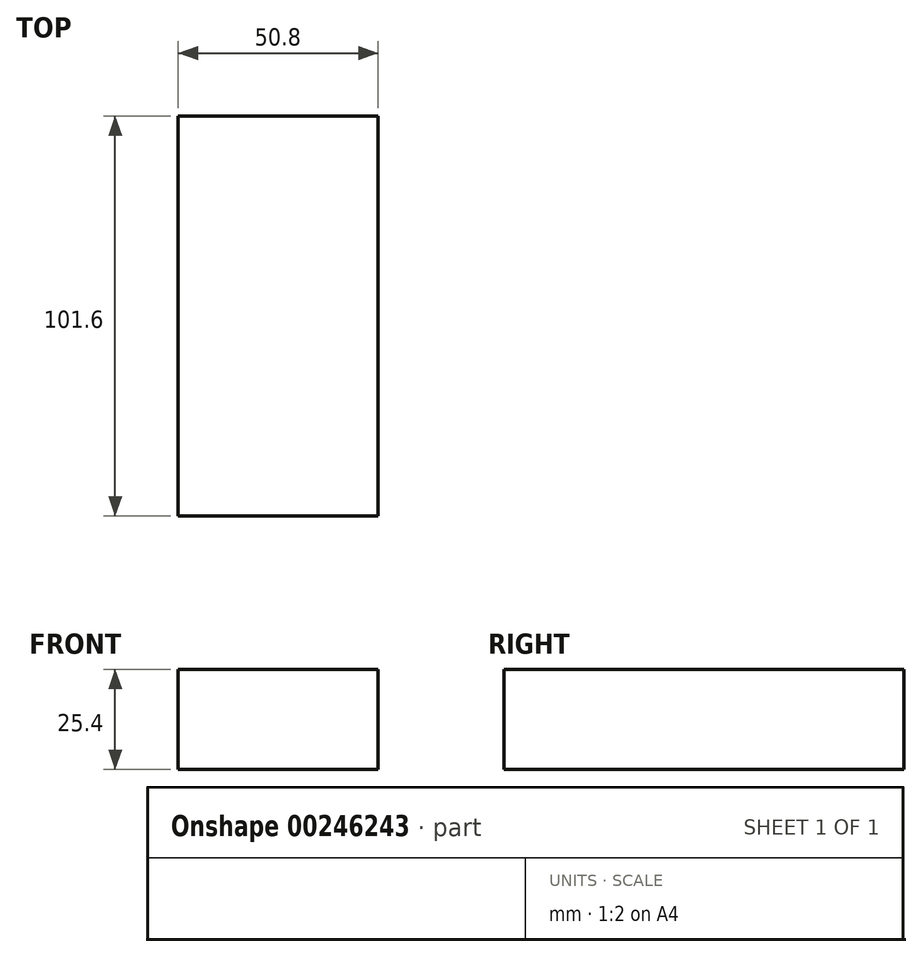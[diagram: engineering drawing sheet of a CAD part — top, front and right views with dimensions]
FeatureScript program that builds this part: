
annotation { "Feature Type Name" : "Feature", "Feature Type Description" : "" }
export const myFeature = defineFeature(function(context is Context, id is Id, definition is map)
    precondition{}
    {
        {
            var Q0;
            Q0=qCreatedBy(makeId("Front.planeOp"),FACE);
            var sketch = newSketch(context, id + "F0", { "sketchPlane" : qUnion([Q0])});
            skLineSegment(sketch, "E0.bottom", {"start": v(0, 0) * mm, "end": v(50.8, 0) * mm});
            skLineSegment(sketch, "E0.top", {"start": v(0, -25.4) * mm, "end": v(50.8, -25.4) * mm});
            skLineSegment(sketch, "E0.left", {"start": v(0, 0) * mm, "end": v(0, -25.4) * mm});
            skLineSegment(sketch, "E0.right", {"start": v(50.8, 0) * mm, "end": v(50.8, -25.4) * mm});
            skSolve(sketch);
        }
        {
            var Q0;
            Q0 = qSketchRegion(id + "F0", true);
            extrude(context, id + "F1", {"entities" : qUnion([Q0]), "depth" : 101.6 * mm});
        }
        {
            var Q0;
            Q0=makeQuery(id+"F1.opExtrude","SWEPT_FACE",FACE,{"disambiguationData":[OSD([sQuery(id+"F0.wireOp",EDGE,"E0.top")])]});
            extrude(context, id + "F2", {"entities" : qUnion([Q0]), "operationType" : NewBodyOperationType.REMOVE, "endBound" : BoundingType.THROUGH_ALL, "depth" : 25.4 * mm});
        }
    });
